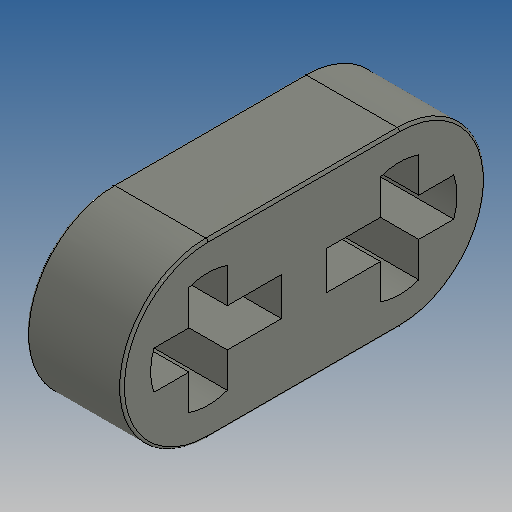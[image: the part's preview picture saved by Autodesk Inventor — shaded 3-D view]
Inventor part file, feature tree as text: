
AUTODESK INVENTOR PART (.ipt)
format: ipt  version: 2025 (Build 290162010, 162A)  size: 168,960 bytes
history: native  units: mm
features: extrude x1, fillet x1, sketch x1
ambient origin geometry x8: Origin, YZ Plane, XZ Plane, XY Plane, X Axis, Y Axis, Z Axis, Center Point
bodies: Solid1 (feature_tree)
feature tree (3):
  extrude  "Extrusion4"  Depth=7.2mm
  fillet  "Fillet1"  Radius=1.6mm
  sketch  "Sketch3"  dims[d15=4.0mm d16=0.0mm d47=4.8mm d49=7.2mm d53=1.6mm d56=0.1mm d57=0.8mm d58=8.0mm]
